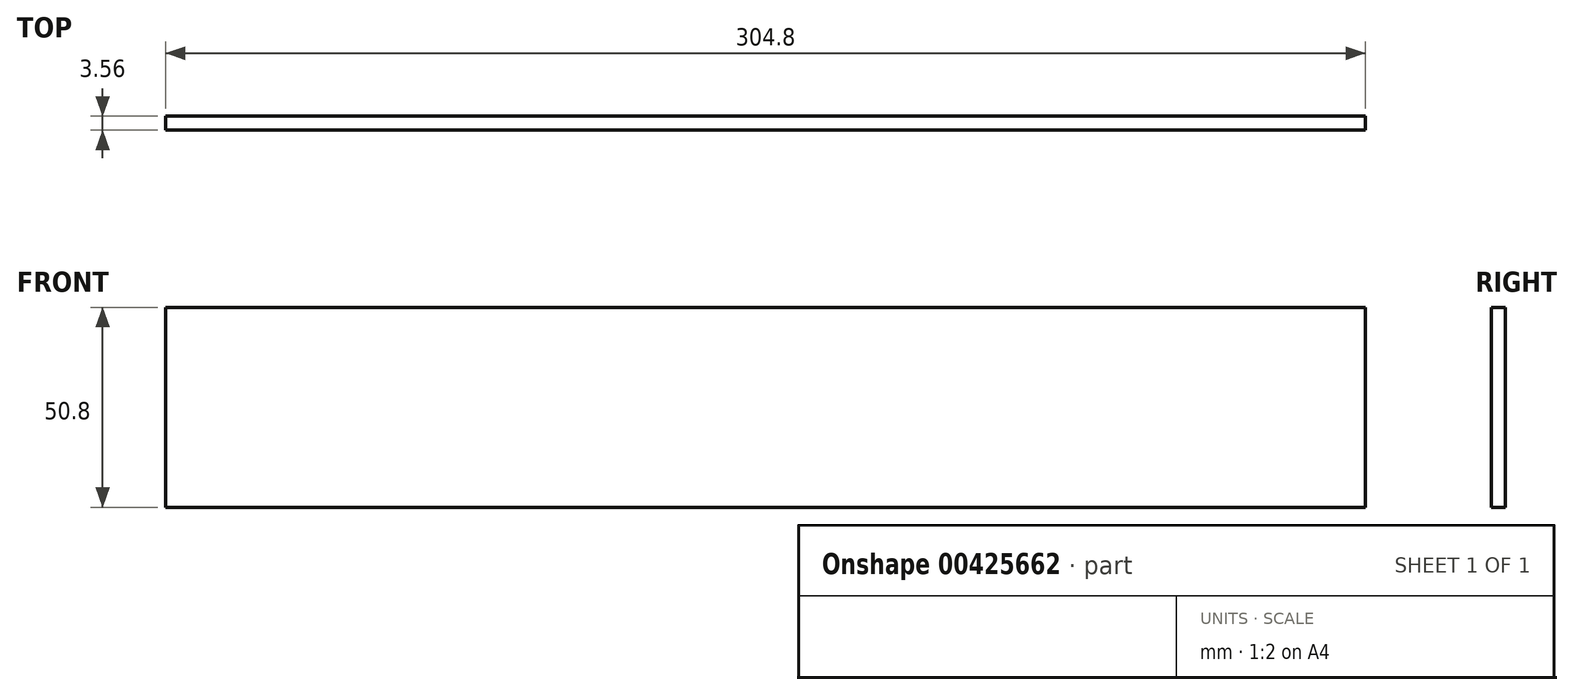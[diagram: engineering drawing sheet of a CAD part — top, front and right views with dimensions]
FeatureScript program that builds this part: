
annotation { "Feature Type Name" : "Feature", "Feature Type Description" : "" }
export const myFeature = defineFeature(function(context is Context, id is Id, definition is map)
    precondition{}
    {
        {
            var Q0;
            Q0=qCreatedBy(makeId("Front.planeOp"),FACE);
            var sketch = newSketch(context, id + "F0", { "sketchPlane" : qUnion([Q0])});
            skLineSegment(sketch, "E0.bottom", {"start": v(-135.77, -36.45) * mm, "end": v(169.03, -36.45) * mm});
            skLineSegment(sketch, "E0.top", {"start": v(-135.77, 14.35) * mm, "end": v(169.03, 14.35) * mm});
            skLineSegment(sketch, "E0.left", {"start": v(-135.77, -36.45) * mm, "end": v(-135.77, 14.35) * mm});
            skLineSegment(sketch, "E0.right", {"start": v(169.03, -36.45) * mm, "end": v(169.03, 14.35) * mm});
            skSolve(sketch);
        }
        {
            var Q0;
            Q0=makeQuery(id+"F0.imprint","IMPRINT",FACE,{"disambiguationData":[TD([[makeQuery(id+"F0.imprint","IMPRINT",EDGE,{"derivedFrom":sQuery(id+"F0.wireOp",EDGE,"E0.bottom")}),1.0]])]});
            extrude(context, id + "F1", {"entities" : qUnion([Q0]), "depth" : 3.56 * mm});
        }
    });
